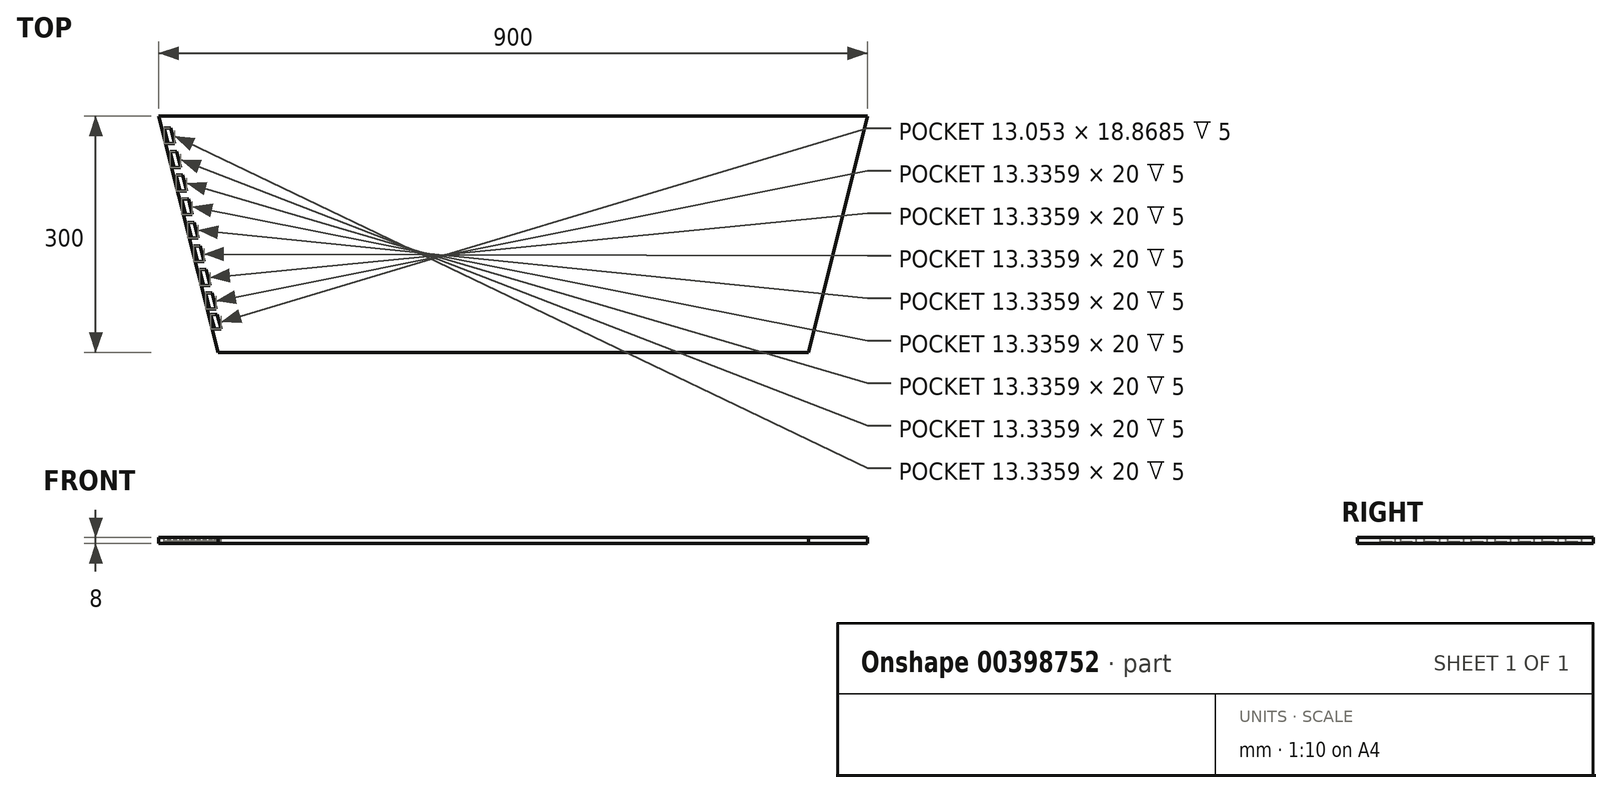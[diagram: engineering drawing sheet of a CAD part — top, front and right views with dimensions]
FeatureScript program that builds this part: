
annotation { "Feature Type Name" : "Feature", "Feature Type Description" : "" }
export const myFeature = defineFeature(function(context is Context, id is Id, definition is map)
    precondition{}
    {
        {
            var Q0;
            Q0=qCreatedBy(makeId("Top.planeOp"),FACE);
            var sketch = newSketch(context, id + "F0", { "sketchPlane" : qUnion([Q0])});
            skLineSegment(sketch, "E0", {"start": v(-413.97, -94.03) * mm, "end": v(336.03, -94.03) * mm});
            skPoint(sketch, "E1.orphan", {"position": v(-413.97, 205.97) * mm});
            skPoint(sketch, "E2.end.orphan", {"position": v(336.03, 205.97) * mm});
            skLineSegment(sketch, "E3", {"start": v(-38.97, 205.97) * mm, "end": v(-488.97, 205.97) * mm});
            skLineSegment(sketch, "E4", {"start": v(-38.97, 205.97) * mm, "end": v(411.03, 205.97) * mm});
            skLineSegment(sketch, "E5", {"start": v(336.03, -94.03) * mm, "end": v(411.03, 205.97) * mm});
            skLineSegment(sketch, "E6", {"start": v(-488.97, 205.97) * mm, "end": v(-413.97, -94.03) * mm});
            skSolve(sketch);
        }
        {
            var Q0;
            Q0=makeQuery(id+"F0.imprint","IMPRINT",FACE,{"disambiguationData":[TD([[makeQuery(id+"F0.imprint","IMPRINT",EDGE,{"derivedFrom":sQuery(id+"F0.wireOp",EDGE,"E0")}),1.0]])]});
            extrude(context, id + "F1", {"entities" : qUnion([Q0]), "depth" : 8 * mm});
        }
        {
            var Q0;
            Q0=makeQuery(id+"F1.opExtrude","CAP_FACE",FACE,{"disambiguationData":[OSD([sQuery(id+"F0.wireOp",EDGE,"E0"),sQuery(id+"F0.wireOp",EDGE,"E3"),sQuery(id+"F0.wireOp",EDGE,"E4"),sQuery(id+"F0.wireOp",EDGE,"E5"),sQuery(id+"F0.wireOp",EDGE,"E6")])],"isStart":false});
            var sketch = newSketch(context, id + "F2", { "sketchPlane" : qUnion([Q0])});
            skLineSegment(sketch, "E7", {"start": v(-413.97, -94.03) * mm, "end": v(-410.97, -94.03) * mm});
            skLineSegment(sketch, "E8", {"start": v(-410.97, -94.03) * mm, "end": v(-485.97, 205.97) * mm});
            skLineSegment(sketch, "E9", {"start": v(-410.97, -94.03) * mm, "end": v(-402.63, -94.03) * mm});
            skLineSegment(sketch, "E10", {"start": v(-402.63, -94.03) * mm, "end": v(-481.5, 221.42) * mm});
            skLineSegment(sketch, "E11", {"start": v(-413.97, -94.03) * mm, "end": v(-443.98, -94.03) * mm});
            skLineSegment(sketch, "E12", {"start": v(-443.98, -94.03) * mm, "end": v(-518.98, 205.97) * mm});
            skLineSegment(sketch, "E13", {"start": v(-443.98, -94.03) * mm, "end": v(-448.83, -74.63) * mm});
            skLineSegment(sketch, "E14", {"start": v(-448.83, -74.63) * mm, "end": v(-196.58, -74.63) * mm});
            skLineSegment(sketch, "E15", {"start": v(-196.58, -74.63) * mm, "end": v(-196.58, -64.63) * mm});
            skLineSegment(sketch, "E16", {"start": v(-196.58, -64.63) * mm, "end": v(-501.48, -64.63) * mm});
            skLineSegment(sketch, "E17", {"start": v(-501.48, -64.63) * mm, "end": v(-501.48, -44.63) * mm});
            skLineSegment(sketch, "E18", {"start": v(-501.48, -44.63) * mm, "end": v(-205.43, -48.9) * mm});
            skLineSegment(sketch, "E19", {"start": v(-205.43, -48.9) * mm, "end": v(-205.28, -38.9) * mm});
            skLineSegment(sketch, "E20", {"start": v(-205.28, -38.9) * mm, "end": v(-506.13, -38.9) * mm});
            skLineSegment(sketch, "E21", {"start": v(-506.13, -38.9) * mm, "end": v(-506.13, -18.9) * mm});
            skLineSegment(sketch, "E22", {"start": v(-506.13, -18.9) * mm, "end": v(-114.73, -18.9) * mm});
            skLineSegment(sketch, "E23", {"start": v(-114.73, -18.9) * mm, "end": v(-114.73, -8.9) * mm});
            skLineSegment(sketch, "E24", {"start": v(-114.73, -8.9) * mm, "end": v(-567.45, -8.9) * mm});
            skLineSegment(sketch, "E25", {"start": v(-567.45, -8.9) * mm, "end": v(-567.45, 11.1) * mm});
            skLineSegment(sketch, "E26", {"start": v(-567.45, 11.1) * mm, "end": v(-101.55, 11.1) * mm});
            skLineSegment(sketch, "E27", {"start": v(-101.55, 11.1) * mm, "end": v(-101.55, 21.1) * mm});
            skLineSegment(sketch, "E28", {"start": v(-101.55, 21.1) * mm, "end": v(-587.23, 21.1) * mm});
            skLineSegment(sketch, "E29", {"start": v(-587.23, 21.1) * mm, "end": v(-587.23, 41.1) * mm});
            skLineSegment(sketch, "E30", {"start": v(-587.23, 41.1) * mm, "end": v(-101.55, 41.1) * mm});
            skLineSegment(sketch, "E31", {"start": v(-101.55, 41.1) * mm, "end": v(-101.55, 51.1) * mm});
            skLineSegment(sketch, "E32", {"start": v(-101.55, 51.1) * mm, "end": v(-590.36, 51.1) * mm});
            skLineSegment(sketch, "E33", {"start": v(-590.36, 51.1) * mm, "end": v(-590.36, 71.1) * mm});
            skLineSegment(sketch, "E34", {"start": v(-590.36, 71.1) * mm, "end": v(-90.01, 71.1) * mm});
            skLineSegment(sketch, "E35", {"start": v(-90.01, 71.1) * mm, "end": v(-90.01, 81.1) * mm});
            skLineSegment(sketch, "E36", {"start": v(-90.01, 81.1) * mm, "end": v(-600.99, 81.1) * mm});
            skLineSegment(sketch, "E37", {"start": v(-600.99, 81.1) * mm, "end": v(-600.99, 101.1) * mm});
            skLineSegment(sketch, "E38", {"start": v(-600.99, 101.1) * mm, "end": v(-131.6, 101.1) * mm});
            skLineSegment(sketch, "E39", {"start": v(-131.6, 101.1) * mm, "end": v(-131.6, 111.1) * mm});
            skLineSegment(sketch, "E40", {"start": v(-131.6, 111.1) * mm, "end": v(-581.12, 111.1) * mm});
            skLineSegment(sketch, "E41", {"start": v(-581.12, 111.1) * mm, "end": v(-581.12, 131.1) * mm});
            skLineSegment(sketch, "E42", {"start": v(-581.12, 131.1) * mm, "end": v(-179.64, 131.1) * mm});
            skLineSegment(sketch, "E43", {"start": v(-179.64, 131.1) * mm, "end": v(-179.64, 141.1) * mm});
            skLineSegment(sketch, "E44", {"start": v(-179.64, 141.1) * mm, "end": v(-540.47, 141.1) * mm});
            skLineSegment(sketch, "E45", {"start": v(-540.47, 141.1) * mm, "end": v(-540.47, 161.1) * mm});
            skLineSegment(sketch, "E46", {"start": v(-540.47, 161.1) * mm, "end": v(-208.29, 161.1) * mm});
            skLineSegment(sketch, "E47", {"start": v(-208.29, 161.1) * mm, "end": v(-208.29, 171.1) * mm});
            skLineSegment(sketch, "E48", {"start": v(-208.29, 171.1) * mm, "end": v(-534.46, 171.1) * mm});
            skLineSegment(sketch, "E49", {"start": v(-534.46, 171.1) * mm, "end": v(-534.46, 191.1) * mm});
            skLineSegment(sketch, "E50", {"start": v(-534.46, 191.1) * mm, "end": v(-224.92, 191.1) * mm});
            skLineSegment(sketch, "E51", {"start": v(-224.92, 191.1) * mm, "end": v(-224.92, 201.1) * mm});
            skLineSegment(sketch, "E52", {"start": v(-224.92, 201.1) * mm, "end": v(-530.3, 201.1) * mm});
            skSolve(sketch);
        }
        {
            var Q0;
            {var subQ0=sQuery(id+"F2.wireOp",EDGE,"E48");var subQ1=sQuery(id+"F2.wireOp",EDGE,"E8");var subQ2=makeQuery(id+"F2.imprint","INTERSECT",VERTEX,{"derivedFrom":[subQ1,subQ0]});Q0=makeQuery(id+"F2.imprint","IMPRINT",FACE,{"disambiguationData":[TD([[makeQuery(id+"F2.imprint","IMPRINT",EDGE,{"disambiguationData":[TD([[subQ2,-1.0]])],"derivedFrom":subQ1}),-1.0]])]});}
            var Q1;
            {var subQ0=sQuery(id+"F2.wireOp",EDGE,"E44");var subQ1=sQuery(id+"F2.wireOp",EDGE,"E8");var subQ2=makeQuery(id+"F2.imprint","INTERSECT",VERTEX,{"derivedFrom":[subQ1,subQ0]});Q1=makeQuery(id+"F2.imprint","IMPRINT",FACE,{"disambiguationData":[TD([[makeQuery(id+"F2.imprint","IMPRINT",EDGE,{"disambiguationData":[TD([[subQ2,-1.0]])],"derivedFrom":subQ1}),-1.0]])]});}
            var Q2;
            {var subQ0=sQuery(id+"F2.wireOp",EDGE,"E40");var subQ1=sQuery(id+"F2.wireOp",EDGE,"E8");var subQ2=makeQuery(id+"F2.imprint","INTERSECT",VERTEX,{"derivedFrom":[subQ1,subQ0]});Q2=makeQuery(id+"F2.imprint","IMPRINT",FACE,{"disambiguationData":[TD([[makeQuery(id+"F2.imprint","IMPRINT",EDGE,{"disambiguationData":[TD([[subQ2,-1.0]])],"derivedFrom":subQ1}),-1.0]])]});}
            var Q3;
            {var subQ0=sQuery(id+"F2.wireOp",EDGE,"E36");var subQ1=sQuery(id+"F2.wireOp",EDGE,"E8");var subQ2=makeQuery(id+"F2.imprint","INTERSECT",VERTEX,{"derivedFrom":[subQ1,subQ0]});Q3=makeQuery(id+"F2.imprint","IMPRINT",FACE,{"disambiguationData":[TD([[makeQuery(id+"F2.imprint","IMPRINT",EDGE,{"disambiguationData":[TD([[subQ2,-1.0]])],"derivedFrom":subQ1}),-1.0]])]});}
            var Q4;
            {var subQ0=sQuery(id+"F2.wireOp",EDGE,"E32");var subQ1=sQuery(id+"F2.wireOp",EDGE,"E8");var subQ2=makeQuery(id+"F2.imprint","INTERSECT",VERTEX,{"derivedFrom":[subQ1,subQ0]});Q4=makeQuery(id+"F2.imprint","IMPRINT",FACE,{"disambiguationData":[TD([[makeQuery(id+"F2.imprint","IMPRINT",EDGE,{"disambiguationData":[TD([[subQ2,-1.0]])],"derivedFrom":subQ1}),-1.0]])]});}
            var Q5;
            {var subQ0=sQuery(id+"F2.wireOp",EDGE,"E28");var subQ1=sQuery(id+"F2.wireOp",EDGE,"E8");var subQ2=makeQuery(id+"F2.imprint","INTERSECT",VERTEX,{"derivedFrom":[subQ1,subQ0]});Q5=makeQuery(id+"F2.imprint","IMPRINT",FACE,{"disambiguationData":[TD([[makeQuery(id+"F2.imprint","IMPRINT",EDGE,{"disambiguationData":[TD([[subQ2,-1.0]])],"derivedFrom":subQ1}),-1.0]])]});}
            var Q6;
            {var subQ0=sQuery(id+"F2.wireOp",EDGE,"E24");var subQ1=sQuery(id+"F2.wireOp",EDGE,"E8");var subQ2=makeQuery(id+"F2.imprint","INTERSECT",VERTEX,{"derivedFrom":[subQ1,subQ0]});Q6=makeQuery(id+"F2.imprint","IMPRINT",FACE,{"disambiguationData":[TD([[makeQuery(id+"F2.imprint","IMPRINT",EDGE,{"disambiguationData":[TD([[subQ2,-1.0]])],"derivedFrom":subQ1}),-1.0]])]});}
            var Q7;
            {var subQ0=sQuery(id+"F2.wireOp",EDGE,"E20");var subQ1=sQuery(id+"F2.wireOp",EDGE,"E8");var subQ2=makeQuery(id+"F2.imprint","INTERSECT",VERTEX,{"derivedFrom":[subQ1,subQ0]});Q7=makeQuery(id+"F2.imprint","IMPRINT",FACE,{"disambiguationData":[TD([[makeQuery(id+"F2.imprint","IMPRINT",EDGE,{"disambiguationData":[TD([[subQ2,-1.0]])],"derivedFrom":subQ1}),-1.0]])]});}
            var Q8;
            {var subQ0=sQuery(id+"F2.wireOp",EDGE,"E16");var subQ1=sQuery(id+"F2.wireOp",EDGE,"E8");var subQ2=makeQuery(id+"F2.imprint","INTERSECT",VERTEX,{"derivedFrom":[subQ1,subQ0]});Q8=makeQuery(id+"F2.imprint","IMPRINT",FACE,{"disambiguationData":[TD([[makeQuery(id+"F2.imprint","IMPRINT",EDGE,{"disambiguationData":[TD([[subQ2,-1.0]])],"derivedFrom":subQ1}),-1.0]])]});}
            extrude(context, id + "F3", {"entities" : qUnion([Q0, Q1, Q2, Q3, Q4, Q5, Q6, Q7, Q8]), "operationType" : NewBodyOperationType.REMOVE, "oppositeDirection" : true, "depth" : 5 * mm});
        }
    });
